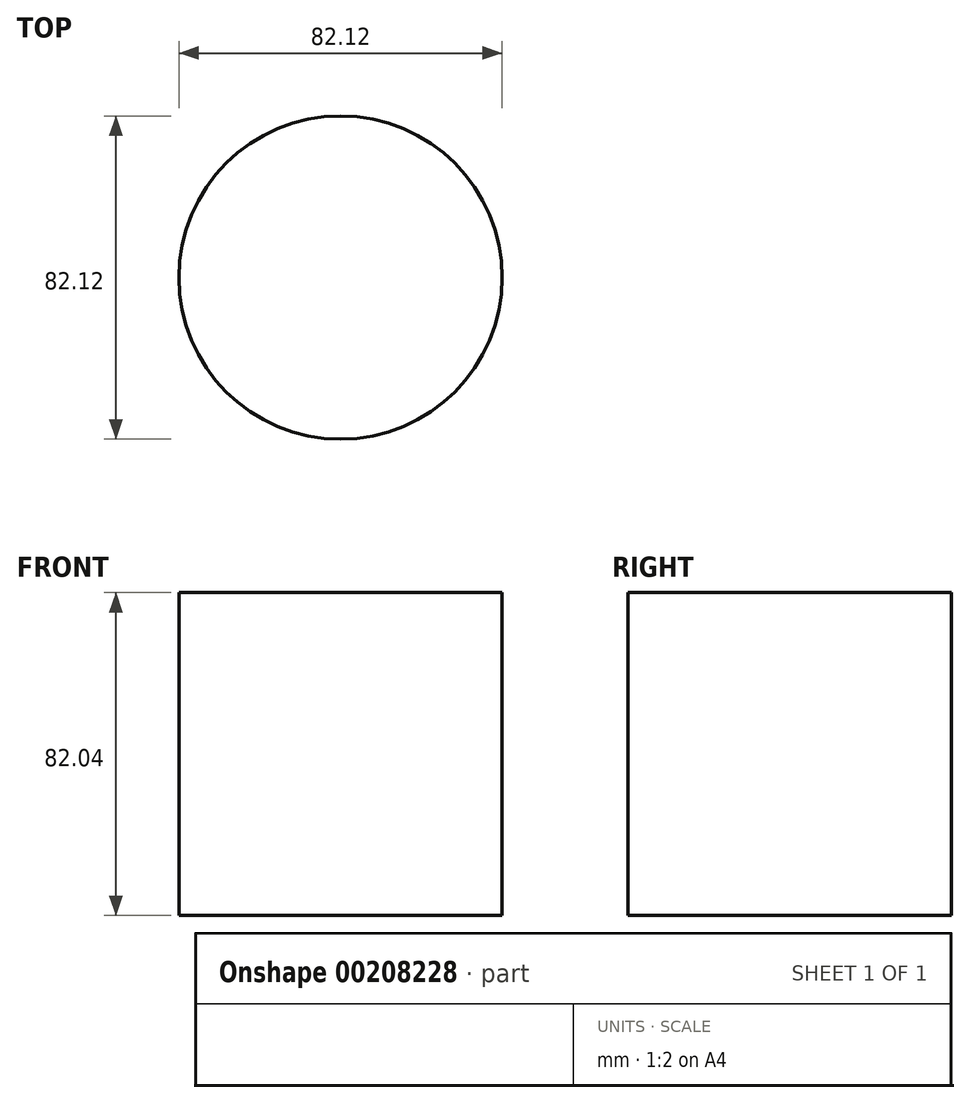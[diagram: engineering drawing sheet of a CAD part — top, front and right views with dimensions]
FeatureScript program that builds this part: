
annotation { "Feature Type Name" : "Feature", "Feature Type Description" : "" }
export const myFeature = defineFeature(function(context is Context, id is Id, definition is map)
    precondition{}
    {
        {
            var Q0;
            Q0=qCreatedBy(makeId("Top.planeOp"),FACE);
            var sketch = newSketch(context, id + "F0", { "sketchPlane" : qUnion([Q0])});
            skCircle(sketch, "E0", {"center": v(0, 0) * mm, "radius": 41.06 * mm});
            skSolve(sketch);
        }
        {
            var Q0;
            Q0=makeQuery(id+"F0.imprint","IMPRINT",FACE,{"disambiguationData":[TD([[makeQuery(id+"F0.imprint","IMPRINT",EDGE,{"derivedFrom":sQuery(id+"F0.wireOp",EDGE,"E0")}),1.0]])]});
            extrude(context, id + "F1", {"entities" : qUnion([Q0]), "depth" : 82.04 * mm});
        }
    });
